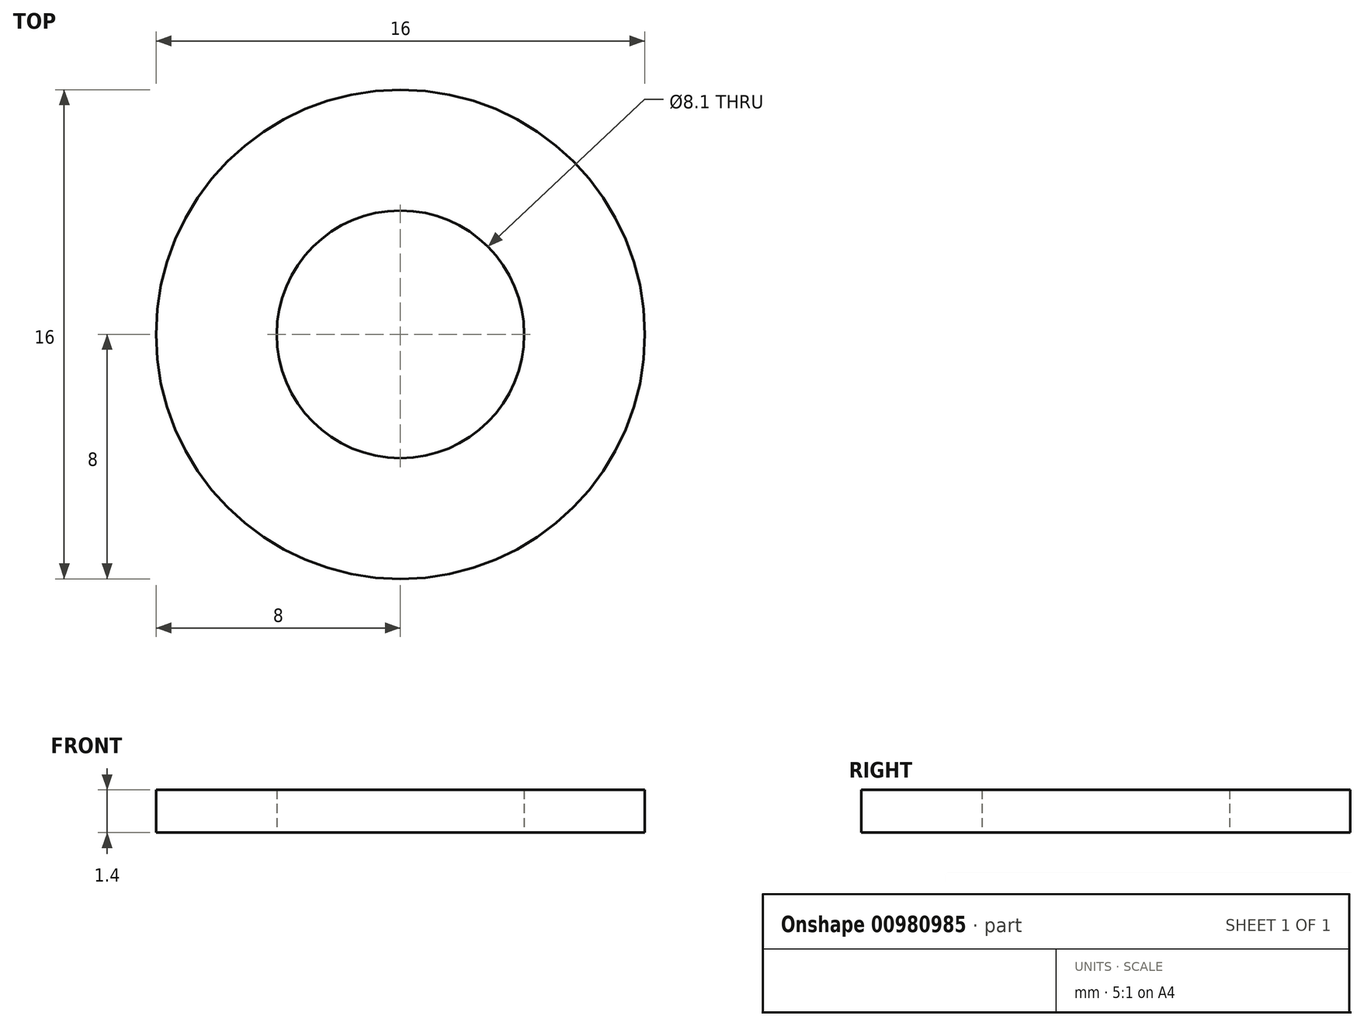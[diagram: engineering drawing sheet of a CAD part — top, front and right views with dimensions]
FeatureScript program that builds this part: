
annotation { "Feature Type Name" : "Feature", "Feature Type Description" : "" }
export const myFeature = defineFeature(function(context is Context, id is Id, definition is map)
    precondition{}
    {
        {
            var Q0;
            Q0=qCreatedBy(makeId("Top.planeOp"),FACE);
            var sketch = newSketch(context, id + "F0", { "sketchPlane" : qUnion([Q0])});
            skCircle(sketch, "E0", {"center": v(0, 0) * mm, "radius": 4.05 * mm});
            skCircle(sketch, "E1", {"center": v(0, 0) * mm, "radius": 8 * mm});
            skSolve(sketch);
        }
        {
            var Q0;
            Q0=makeQuery(id+"F0.imprint","IMPRINT",FACE,{"disambiguationData":[TD([[makeQuery(id+"F0.imprint","IMPRINT",EDGE,{"derivedFrom":sQuery(id+"F0.wireOp",EDGE,"E0")}),-1.0]])]});
            extrude(context, id + "F1", {"entities" : qUnion([Q0]), "depth" : 1.4 * mm, "offsetDistance" : 25 * mm});
        }
    });
